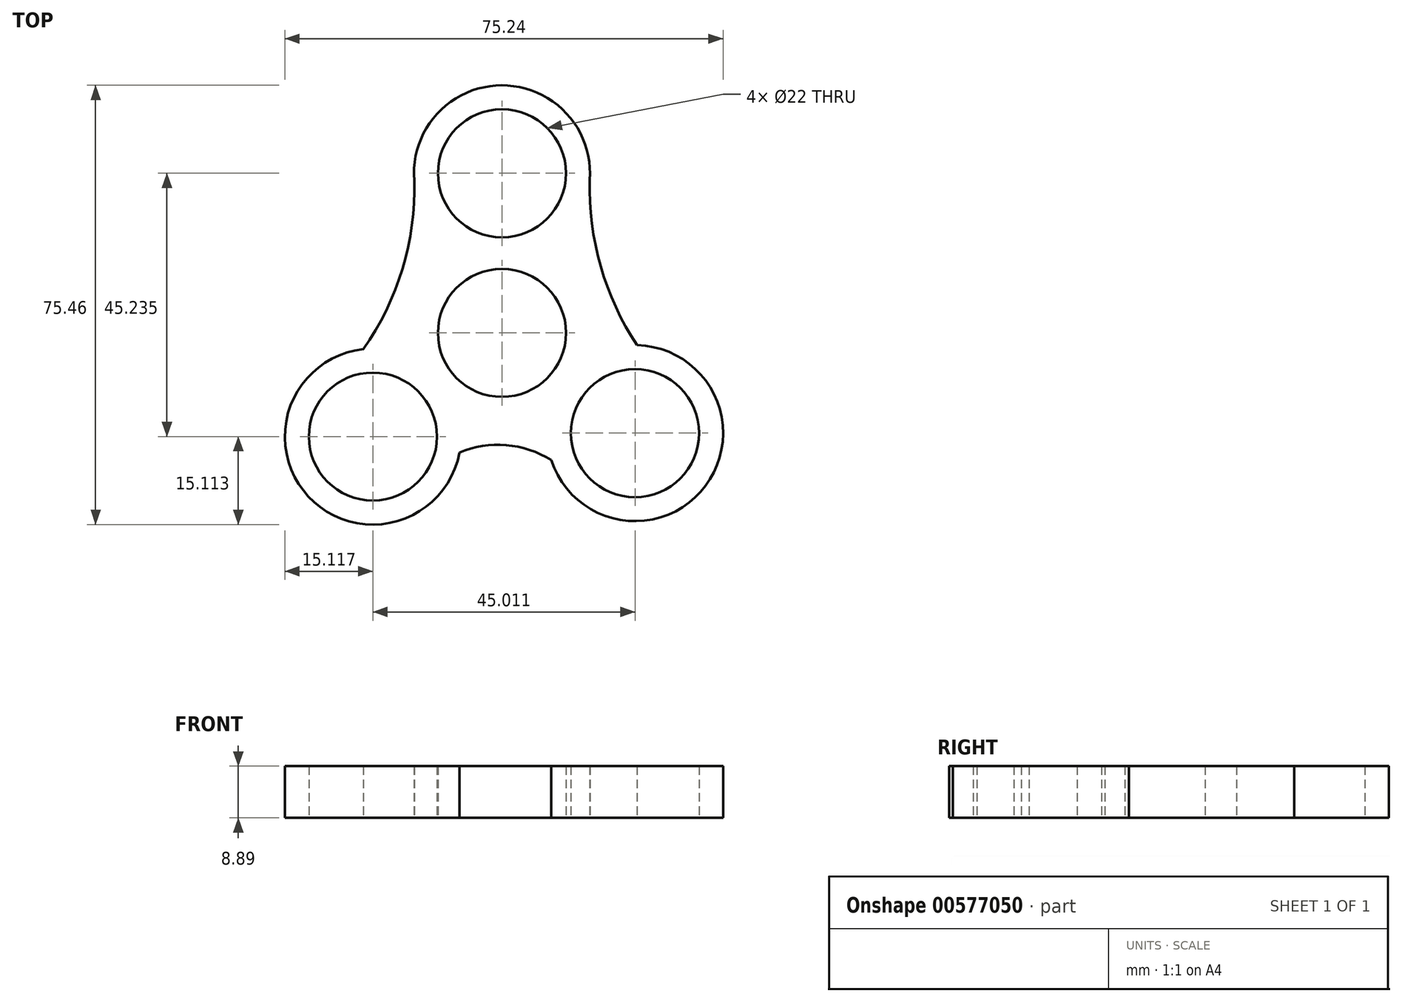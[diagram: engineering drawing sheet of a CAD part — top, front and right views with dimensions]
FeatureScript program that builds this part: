
annotation { "Feature Type Name" : "Feature", "Feature Type Description" : "" }
export const myFeature = defineFeature(function(context is Context, id is Id, definition is map)
    precondition{}
    {
        {
            var Q0;
            Q0=qCreatedBy(makeId("Top.planeOp"),FACE);
            var sketch = newSketch(context, id + "F0", { "sketchPlane" : qUnion([Q0])});
            skCircle(sketch, "E0", {"center": v(0, 0) * mm, "radius": 11 * mm});
            skCircle(sketch, "E1", {"center": v(0, 27.42) * mm, "radius": 11 * mm});
            skCircle(sketch, "E2", {"center": v(-22.16, -17.82) * mm, "radius": 11 * mm});
            skCircle(sketch, "E3", {"center": v(22.85, -17.22) * mm, "radius": 11 * mm});
            skCircle(sketch, "E4", {"center": v(-22.16, -17.82) * mm, "radius": 15.11 * mm});
            skCircle(sketch, "E5", {"center": v(22.85, -17.22) * mm, "radius": 15.11 * mm});
            skCircle(sketch, "E6", {"center": v(0, 27.42) * mm, "radius": 15.11 * mm});
            skArc(sketch, "E7", {"start": v(-23.82, -2.8) * mm, "mid": v(-16.92, 11.58) * mm, "end": v(-15.11, 27.42) * mm});
            skArc(sketch, "E8", {"start": v(15.11, 27.42) * mm, "mid": v(16.8, 12.01) * mm, "end": v(23.2, -2.1) * mm});
            skArc(sketch, "E9", {"start": v(8.46, -21.86) * mm, "mid": v(0.74, -19.27) * mm, "end": v(-7.3, -20.59) * mm});
            skSolve(sketch);
        }
        {
            var Q0;
            Q0=qSketchRegion(id+"F0",true);
            extrude(context, id + "F1", {"entities" : qUnion([Q0]), "depth" : 8.9 * mm, "offsetDistance" : 25.4 * mm});
        }
    });
